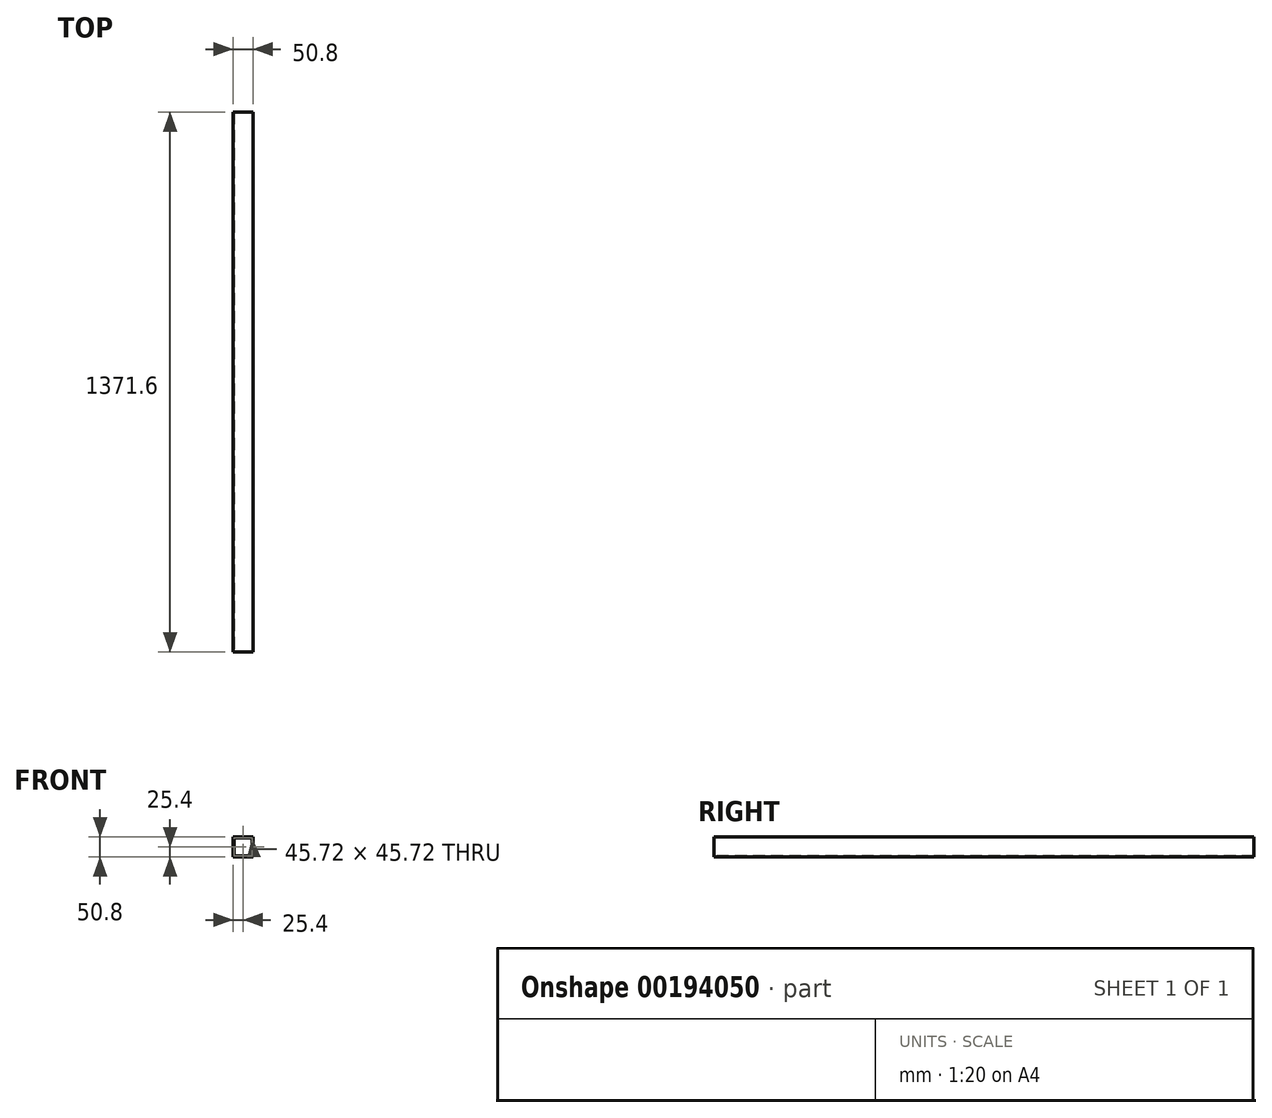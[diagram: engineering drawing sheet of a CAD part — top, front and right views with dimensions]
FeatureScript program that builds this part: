
annotation { "Feature Type Name" : "Feature", "Feature Type Description" : "" }
export const myFeature = defineFeature(function(context is Context, id is Id, definition is map)
    precondition{}
    {
        {
            var Q0;
            Q0=qCreatedBy(makeId("Right.planeOp"),FACE);
            var sketch = newSketch(context, id + "F0", { "sketchPlane" : qUnion([Q0])});
            skLineSegment(sketch, "E0.bottom", {"start": v(685.8, -25.4) * mm, "end": v(-685.8, -25.4) * mm});
            skLineSegment(sketch, "E0.top", {"start": v(685.8, 25.4) * mm, "end": v(-685.8, 25.4) * mm});
            skLineSegment(sketch, "E0.left", {"start": v(685.8, -25.4) * mm, "end": v(685.8, 25.4) * mm});
            skLineSegment(sketch, "E0.right", {"start": v(-685.8, -25.4) * mm, "end": v(-685.8, 25.4) * mm});
            skPoint(sketch, "E0.middle", {"position": v(0, 0) * mm});
            skSolve(sketch);
        }
        {
            var Q0;
            Q0 = qSketchRegion(id + "F0", true);
            extrude(context, id + "F1", {"entities" : qUnion([Q0]), "depth" : 50.8 * mm});
        }
        {
            var Q0;
            Q0=makeQuery(id+"F1.opExtrude","SWEPT_FACE",FACE,{"disambiguationData":[OSD([sQuery(id+"F0.wireOp",EDGE,"E0.right")])]});
            var Q1;
            Q1=makeQuery(id+"F1.opExtrude","SWEPT_FACE",FACE,{"disambiguationData":[OSD([sQuery(id+"F0.wireOp",EDGE,"E0.left")])]});
            shell(context, id + "F2", {"entities" : qUnion([Q0, Q1]), "thickness" : 2.54 * mm});
        }
    });
